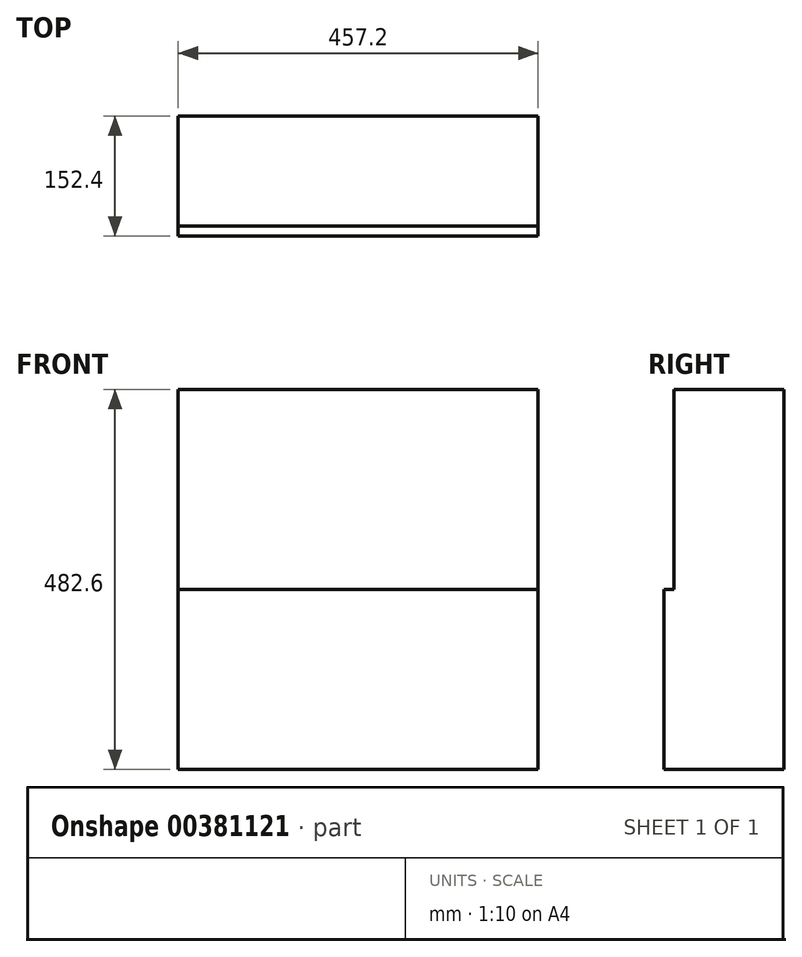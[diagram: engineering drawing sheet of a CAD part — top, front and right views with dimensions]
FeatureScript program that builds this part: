
annotation { "Feature Type Name" : "Feature", "Feature Type Description" : "" }
export const myFeature = defineFeature(function(context is Context, id is Id, definition is map)
    precondition{}
    {
        {
            var Q0;
            Q0=qCreatedBy(makeId("Front.planeOp"),FACE);
            var sketch = newSketch(context, id + "F0", { "sketchPlane" : qUnion([Q0])});
            skLineSegment(sketch, "E0.bottom", {"start": v(-228.6, 228.6) * mm, "end": v(228.6, 228.6) * mm});
            skLineSegment(sketch, "E0.top", {"start": v(-228.6, -228.6) * mm, "end": v(228.6, -228.6) * mm});
            skLineSegment(sketch, "E0.left", {"start": v(-228.6, 228.6) * mm, "end": v(-228.6, -228.6) * mm});
            skLineSegment(sketch, "E0.right", {"start": v(228.6, 228.6) * mm, "end": v(228.6, -228.6) * mm});
            skPoint(sketch, "E0.middle", {"position": v(0, 0) * mm});
            skSolve(sketch);
        }
        {
            var Q0;
            Q0=makeQuery(id+"F0.imprint","IMPRINT",FACE,{"disambiguationData":[TD([[makeQuery(id+"F0.imprint","IMPRINT",EDGE,{"derivedFrom":sQuery(id+"F0.wireOp",EDGE,"E0.bottom")}),-1.0]])]});
            extrude(context, id + "F1", {"entities" : qUnion([Q0]), "depth" : 152.4 * mm});
        }
        {
            var Q0;
            Q0=makeQuery(id+"F1.opExtrude","CAP_FACE",FACE,{"disambiguationData":[OSD([sQuery(id+"F0.wireOp",EDGE,"E0.bottom"),sQuery(id+"F0.wireOp",EDGE,"E0.top"),sQuery(id+"F0.wireOp",EDGE,"E0.left"),sQuery(id+"F0.wireOp",EDGE,"E0.right")])],"isStart":false});
            var sketch = newSketch(context, id + "F2", { "sketchPlane" : qUnion([Q0])});
            skLineSegment(sketch, "E1.bottom", {"start": v(-228.6, 228.6) * mm, "end": v(228.6, 228.6) * mm});
            skLineSegment(sketch, "E1.top", {"start": v(-228.6, 0) * mm, "end": v(228.6, 0) * mm});
            skLineSegment(sketch, "E1.left", {"start": v(-228.6, 228.6) * mm, "end": v(-228.6, 0) * mm});
            skLineSegment(sketch, "E1.right", {"start": v(228.6, 228.6) * mm, "end": v(228.6, 0) * mm});
            skSolve(sketch);
        }
        {
            var Q0;
            Q0=makeQuery(id+"F2.imprint","IMPRINT",FACE,{"disambiguationData":[TD([[makeQuery(id+"F2.imprint","IMPRINT",EDGE,{"derivedFrom":sQuery(id+"F2.wireOp",EDGE,"E1.bottom")}),-1.0]])]});
            extrude(context, id + "F3", {"entities" : qUnion([Q0]), "operationType" : NewBodyOperationType.REMOVE, "oppositeDirection" : true, "depth" : 12.7 * mm});
        }
        {
            var Q0;
            Q0=makeQuery(id+"F1.opExtrude","SWEPT_FACE",FACE,{"disambiguationData":[OSD([sQuery(id+"F0.wireOp",EDGE,"E0.bottom")])]});
            var sketch = newSketch(context, id + "F4", { "sketchPlane" : qUnion([Q0])});
            skSolve(sketch);
        }
        {
            var Q0;
            {var subQ0=sQuery(id+"F0.wireOp",EDGE,"E0.bottom");Q0=makeQuery(id+"F4.imprint","IMPRINT",FACE,{"disambiguationData":[TD([[makeQuery(id+"F4.imprint","IMPRINT",EDGE,{"derivedFrom":makeQuery(id+"F1.opExtrude","CAP_EDGE",EDGE,{"disambiguationData":[OSD([subQ0])],"isStart":true})}),-1.0]])]});}
            extrude(context, id + "F5", {"entities" : qUnion([Q0]), "operationType" : NewBodyOperationType.ADD, "depth" : 25.4 * mm});
        }
    });
